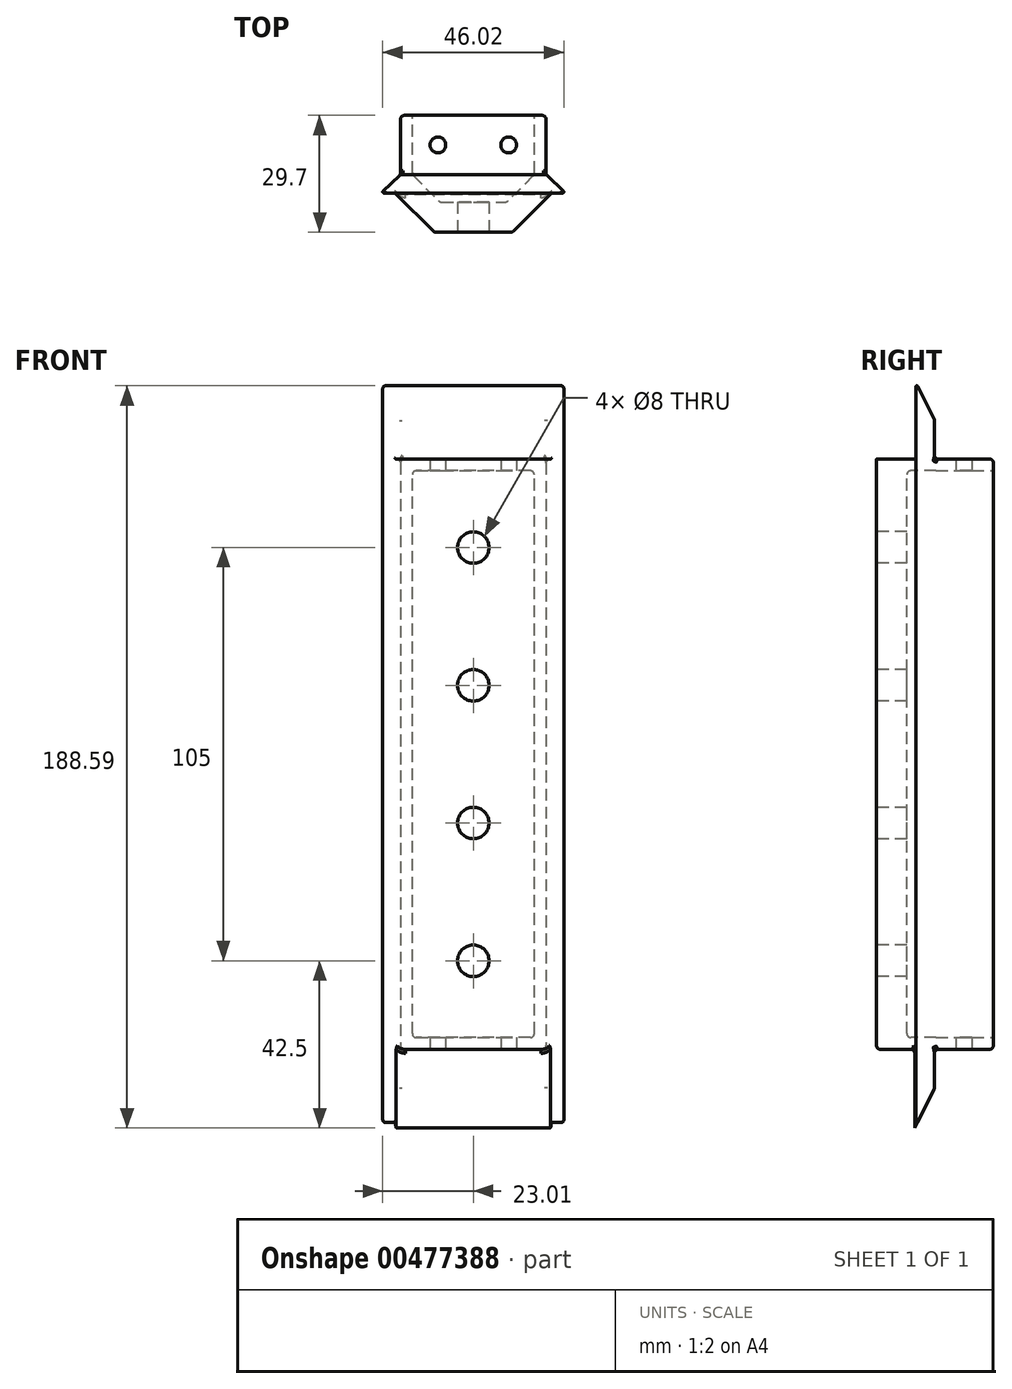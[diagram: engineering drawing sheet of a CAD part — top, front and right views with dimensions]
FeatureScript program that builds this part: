
annotation { "Feature Type Name" : "Feature", "Feature Type Description" : "" }
export const myFeature = defineFeature(function(context is Context, id is Id, definition is map)
    precondition{}
    {
        {
            var Q0;
            Q0=qCreatedBy(makeId("Top.planeOp"),FACE);
            var sketch = newSketch(context, id + "F0", { "sketchPlane" : qUnion([Q0])});
            skLineSegment(sketch, "E0", {"start": v(0, 37.2) * mm, "end": v(0, -38.8) * mm, "construction": true});
            skLineSegment(sketch, "E1", {"start": v(-30.9, 0) * mm, "end": v(40.1, 0) * mm, "construction": true});
            skLineSegment(sketch, "E2.bottom", {"start": v(-18.5, 2.5) * mm, "end": v(18.5, 2.5) * mm});
            skLineSegment(sketch, "E2.top", {"start": v(-23.69, -2.5) * mm, "end": v(23.69, -2.5) * mm});
            skLineSegment(sketch, "E3", {"start": v(-23.69, -2.5) * mm, "end": v(-18.5, 2.5) * mm});
            skLineSegment(sketch, "E4.MirrorCS", {"start": v(23.69, -2.5) * mm, "end": v(18.5, 2.5) * mm});
            skSolve(sketch);
        }
        {
            var Q0;
            Q0 = qSketchRegion(id + "F0", true);
            extrude(context, id + "F1", {"entities" : qUnion([Q0]), "depth" : 170 * mm, "symmetric" : true});
        }
        {
            var Q0;
            Q0=makeQuery(id+"F1.opExtrude","CAP_FACE",FACE,{"disambiguationData":[OSD([sQuery(id+"F0.wireOp",EDGE,"E2.bottom"),sQuery(id+"F0.wireOp",EDGE,"E2.top"),sQuery(id+"F0.wireOp",EDGE,"E3"),sQuery(id+"F0.wireOp",EDGE,"E4.MirrorCS")])],"isStart":false});
            var sketch = newSketch(context, id + "F2", { "sketchPlane" : qUnion([Q0])});
            skLineSegment(sketch, "E5", {"start": v(0, 54.86) * mm, "end": v(0, -60.8) * mm, "construction": true});
            skPoint(sketch, "E5.endSnap0", {"position": v(0, -2.5) * mm});
            skLineSegment(sketch, "E6", {"start": v(20, 2.5) * mm, "end": v(10, 12.5) * mm, "construction": true});
            skLineSegment(sketch, "E7", {"start": v(10, 12.5) * mm, "end": v(0, 12.5) * mm, "construction": true});
            skLineSegment(sketch, "E8.0", {"start": v(-20, 2.5) * mm, "end": v(20, 2.5) * mm, "construction": true});
            skLineSegment(sketch, "E9.MirrorCS", {"start": v(-20, 2.5) * mm, "end": v(-10, 12.5) * mm, "construction": true});
            skLineSegment(sketch, "E10.MirrorCS", {"start": v(-10, 12.5) * mm, "end": v(0, 12.5) * mm, "construction": true});
            skPoint(sketch, "E11.orphan", {"position": v(18.5, 2.5) * mm});
            skPoint(sketch, "E12.orphan", {"position": v(-18.5, 2.5) * mm});
            skLineSegment(sketch, "E13", {"start": v(0, 0) * mm, "end": v(27.86, 0) * mm, "construction": true});
            skPoint(sketch, "E13.endSnap0", {"position": v(21.1, 0) * mm});
            skLineSegment(sketch, "E14.MirrorCS", {"start": v(-20, -2.5) * mm, "end": v(-10, -12.5) * mm});
            skLineSegment(sketch, "E15.MirrorCS", {"start": v(-20, -2.5) * mm, "end": v(20, -2.5) * mm});
            skLineSegment(sketch, "E16.MirrorCS", {"start": v(10, -12.5) * mm, "end": v(0, -12.5) * mm});
            skLineSegment(sketch, "E17.MirrorCS", {"start": v(-10, -12.5) * mm, "end": v(0, -12.5) * mm});
            skLineSegment(sketch, "E18.MirrorCS", {"start": v(20, -2.5) * mm, "end": v(10, -12.5) * mm});
            skPoint(sketch, "E19.MirrorP", {"position": v(18.5, -2.5) * mm});
            skSolve(sketch);
        }
        {
            var Q0;
            Q0 = qSketchRegion(id + "F2", true);
            extrude(context, id + "F3", {"entities" : qUnion([Q0]), "operationType" : NewBodyOperationType.ADD, "oppositeDirection" : true, "depth" : 170 * mm});
        }
        {
            var Q0;
            Q0=qCreatedBy(makeId("Right.planeOp"),FACE);
            var sketch = newSketch(context, id + "F4", { "sketchPlane" : qUnion([Q0])});
            skLineSegment(sketch, "E20", {"start": v(0, 0) * mm, "end": v(-132.45, 0) * mm, "construction": true});
            skLineSegment(sketch, "E21.0", {"start": v(2.5, 75) * mm, "end": v(2.5, -75) * mm});
            skLineSegment(sketch, "E22", {"start": v(2.5, 75) * mm, "end": v(17.5, 75) * mm});
            skLineSegment(sketch, "E23", {"start": v(17.5, 75) * mm, "end": v(17.5, 0) * mm});
            skPoint(sketch, "E24.orphan", {"position": v(2.5, 85) * mm});
            skLineSegment(sketch, "E25.MirrorCS", {"start": v(2.5, -75) * mm, "end": v(17.5, -75) * mm});
            skLineSegment(sketch, "E26.MirrorCS", {"start": v(17.5, -75) * mm, "end": v(17.5, 0) * mm});
            skPoint(sketch, "E27.orphan", {"position": v(2.5, -85) * mm});
            skSolve(sketch);
        }
        {
            var Q0;
            Q0 = qSketchRegion(id + "F4", true);
            extrude(context, id + "F5", {"entities" : qUnion([Q0]), "operationType" : NewBodyOperationType.ADD, "depth" : 37 * mm, "symmetric" : true});
        }
        {
            var Q0;
            Q0=makeQuery(id+"F3.opExtrude","SWEPT_FACE",FACE,{"disambiguationData":[OSD([sQuery(id+"F2.wireOp",EDGE,"E16.MirrorCS"),sQuery(id+"F2.wireOp",EDGE,"E17.MirrorCS")])]});
            var sketch = newSketch(context, id + "F6", { "sketchPlane" : qUnion([Q0])});
            skLineSegment(sketch, "E28", {"start": v(0, 85) * mm, "end": v(0, -85) * mm, "construction": true});
            skCircle(sketch, "E29", {"center": v(0, 52.5) * mm, "radius": 4 * mm});
            skCircle(sketch, "E30", {"center": v(0, 17.5) * mm, "radius": 4 * mm});
            skLineSegment(sketch, "E31", {"start": v(-48.17, 0) * mm, "end": v(56.97, 0) * mm, "construction": true});
            skCircle(sketch, "E32.MirrorC", {"center": v(0, -52.5) * mm, "radius": 4 * mm});
            skCircle(sketch, "E33.MirrorC", {"center": v(0, -17.5) * mm, "radius": 4 * mm});
            skSolve(sketch);
        }
        {
            var Q0;
            Q0 = qSketchRegion(id + "F6", true);
            extrude(context, id + "F7", {"entities" : qUnion([Q0]), "operationType" : NewBodyOperationType.REMOVE, "endBound" : BoundingType.THROUGH_ALL, "oppositeDirection" : true, "depth" : 25 * mm});
        }
        {
            var Q0;
            Q0=makeQuery(id+"F5.opExtrude","SWEPT_FACE",FACE,{"disambiguationData":[OSD([sQuery(id+"F4.wireOp",EDGE,"E23"),sQuery(id+"F4.wireOp",EDGE,"E26.MirrorCS")])]});
            var sketch = newSketch(context, id + "F8", { "sketchPlane" : qUnion([Q0])});
            skLineSegment(sketch, "E34.0", {"start": v(-15.5, -72) * mm, "end": v(-15.5, 72) * mm});
            skLineSegment(sketch, "E34.1", {"start": v(-15.5, -72) * mm, "end": v(15.5, -72) * mm});
            skLineSegment(sketch, "E34.2", {"start": v(15.5, -72) * mm, "end": v(15.5, 72) * mm});
            skLineSegment(sketch, "E34.3", {"start": v(-15.5, 72) * mm, "end": v(15.5, 72) * mm});
            skSolve(sketch);
        }
        {
            var Q0;
            Q0 = qSketchRegion(id + "F8", true);
            var Q1;
            {var subQ2=sQuery(id+"F0.wireOp",EDGE,"E2.bottom");var subQ6=sQuery(id+"F4.wireOp",EDGE,"E22");Q1=makeQuery(id+"F5.boolean.opBoolean","SPLIT",FACE,{"disambiguationData":[TD([makeQuery(id+"F5.opExtrude","SWEPT_FACE",FACE,{"disambiguationData":[OSD([subQ6])]})])],"derivedFrom":makeQuery(id+"F1.opExtrude","SWEPT_FACE",FACE,{"disambiguationData":[OSD([subQ2])]})});}
            extrude(context, id + "F9", {"entities" : qUnion([Q0]), "operationType" : NewBodyOperationType.REMOVE, "endBound" : BoundingType.UP_TO_SURFACE, "oppositeDirection" : true, "endBoundEntityFace" : qUnion([Q1]), "depth" : 25 * mm});
        }
        {
            var Q0;
            Q0=makeQuery(id+"F9.boolean.opBoolean","COPY",FACE,{"derivedFrom":makeQuery(id+"F9.opExtrude","SWEPT_FACE",FACE,{"disambiguationData":[OSD([sQuery(id+"F8.wireOp",EDGE,"E34.3")])]})});
            var sketch = newSketch(context, id + "F10", { "sketchPlane" : qUnion([Q0])});
            skLineSegment(sketch, "E35.0", {"start": v(-15.5, -2.5) * mm, "end": v(-8.5, 4.5) * mm});
            skLineSegment(sketch, "E35.2", {"start": v(15.5, -2.5) * mm, "end": v(8.5, 4.5) * mm});
            skLineSegment(sketch, "E36.0", {"start": v(-15.5, -2.5) * mm, "end": v(15.5, -2.5) * mm});
            skPoint(sketch, "E37.orphan", {"position": v(15.5, -2.5) * mm});
            skPoint(sketch, "E38.orphan", {"position": v(-15.5, -2.5) * mm});
            skLineSegment(sketch, "E39.0", {"start": v(-8.5, 4.5) * mm, "end": v(8.5, 4.5) * mm});
            skSolve(sketch);
        }
        {
            var Q0;
            Q0 = qSketchRegion(id + "F10", true);
            var Q1;
            Q1=makeQuery(id+"F9.boolean.opBoolean","COPY",FACE,{"derivedFrom":makeQuery(id+"F9.opExtrude","SWEPT_FACE",FACE,{"disambiguationData":[OSD([sQuery(id+"F8.wireOp",EDGE,"E34.1")])]})});
            extrude(context, id + "F11", {"entities" : qUnion([Q0]), "operationType" : NewBodyOperationType.REMOVE, "endBound" : BoundingType.UP_TO_SURFACE, "endBoundEntityFace" : qUnion([Q1]), "depth" : 25 * mm});
        }
        {
            var Q0;
            Q0=makeQuery(id+"F5.opExtrude","SWEPT_FACE",FACE,{"disambiguationData":[OSD([sQuery(id+"F4.wireOp",EDGE,"E25.MirrorCS")])]});
            var sketch = newSketch(context, id + "F12", { "sketchPlane" : qUnion([Q0])});
            skLineSegment(sketch, "E40.0", {"start": v(-15.5, -2.5) * mm, "end": v(-15.5, -17.5) * mm, "construction": true});
            skLineSegment(sketch, "E40.1", {"start": v(15.5, -2.5) * mm, "end": v(15.5, -17.5) * mm, "construction": true});
            skLineSegment(sketch, "E41", {"start": v(-15.5, -10) * mm, "end": v(15.5, -10) * mm, "construction": true});
            skCircle(sketch, "E42", {"center": v(-9, -10) * mm, "radius": 2 * mm});
            skLineSegment(sketch, "E43", {"start": v(0, -2.5) * mm, "end": v(0, -17.5) * mm, "construction": true});
            skCircle(sketch, "E44.MirrorC", {"center": v(9, -10) * mm, "radius": 2 * mm});
            skCircle(sketch, "E45", {"center": v(9, -10) * mm, "radius": 3.5 * mm, "construction": true});
            skSolve(sketch);
        }
        {
            var Q0;
            Q0=makeQuery(id+"F3.boolean.opBoolean","MERGE",FACE,{"derivedFrom":[makeQuery(id+"F1.opExtrude","CAP_FACE",FACE,{"disambiguationData":[OSD([sQuery(id+"F0.wireOp",EDGE,"E2.bottom"),sQuery(id+"F0.wireOp",EDGE,"E2.top"),sQuery(id+"F0.wireOp",EDGE,"E3"),sQuery(id+"F0.wireOp",EDGE,"E4.MirrorCS")])],"isStart":true}),makeQuery(id+"F3.opExtrude","CAP_FACE",FACE,{"disambiguationData":[OSD([sQuery(id+"F2.wireOp",EDGE,"E14.MirrorCS"),sQuery(id+"F2.wireOp",EDGE,"E15.MirrorCS"),sQuery(id+"F2.wireOp",EDGE,"E16.MirrorCS"),sQuery(id+"F2.wireOp",EDGE,"E17.MirrorCS"),sQuery(id+"F2.wireOp",EDGE,"E18.MirrorCS")])],"isStart":false})]});
            var sketch = newSketch(context, id + "F13", { "sketchPlane" : qUnion([Q0])});
            skLineSegment(sketch, "E46.0", {"start": v(20, 2.5) * mm, "end": v(10, 12.5) * mm});
            skLineSegment(sketch, "E46.1", {"start": v(-10, 12.5) * mm, "end": v(10, 12.5) * mm});
            skLineSegment(sketch, "E46.2", {"start": v(-20, 2.5) * mm, "end": v(-10, 12.5) * mm});
            skPoint(sketch, "E46.3", {"position": v(15, 7.5) * mm});
            skLineSegment(sketch, "E47", {"start": v(20, 2.5) * mm, "end": v(-20, 2.5) * mm});
            skSolve(sketch);
        }
        {
            var Q0;
            Q0 = qSketchRegion(id + "F13", true);
            extrude(context, id + "F14", {"entities" : qUnion([Q0]), "operationType" : NewBodyOperationType.REMOVE, "oppositeDirection" : true, "depth" : 10 * mm});
        }
        {
            var Q0;
            Q0=makeQuery(id+"F3.boolean.opBoolean","MERGE",FACE,{"derivedFrom":[makeQuery(id+"F1.opExtrude","CAP_FACE",FACE,{"disambiguationData":[OSD([sQuery(id+"F0.wireOp",EDGE,"E2.bottom"),sQuery(id+"F0.wireOp",EDGE,"E2.top"),sQuery(id+"F0.wireOp",EDGE,"E3"),sQuery(id+"F0.wireOp",EDGE,"E4.MirrorCS")])],"isStart":false}),makeQuery(id+"F3.opExtrude","CAP_FACE",FACE,{"disambiguationData":[OSD([sQuery(id+"F2.wireOp",EDGE,"E14.MirrorCS"),sQuery(id+"F2.wireOp",EDGE,"E15.MirrorCS"),sQuery(id+"F2.wireOp",EDGE,"E16.MirrorCS"),sQuery(id+"F2.wireOp",EDGE,"E17.MirrorCS"),sQuery(id+"F2.wireOp",EDGE,"E18.MirrorCS")])],"isStart":true})]});
            var sketch = newSketch(context, id + "F15", { "sketchPlane" : qUnion([Q0])});
            skLineSegment(sketch, "E48.0", {"start": v(20, -2.5) * mm, "end": v(10, -12.5) * mm});
            skLineSegment(sketch, "E48.1", {"start": v(-10, -12.5) * mm, "end": v(10, -12.5) * mm});
            skLineSegment(sketch, "E48.2", {"start": v(-20, -2.5) * mm, "end": v(-10, -12.5) * mm});
            skLineSegment(sketch, "E49", {"start": v(20, -2.5) * mm, "end": v(-20, -2.5) * mm});
            skSolve(sketch);
        }
        {
            var Q0;
            Q0 = qSketchRegion(id + "F15", true);
            extrude(context, id + "F16", {"entities" : qUnion([Q0]), "operationType" : NewBodyOperationType.REMOVE, "oppositeDirection" : true, "depth" : 10 * mm});
        }
        {
            var Q0;
            Q0 = qSketchRegion(id + "F12", true);
            extrude(context, id + "F17", {"entities" : qUnion([Q0]), "operationType" : NewBodyOperationType.REMOVE, "endBound" : BoundingType.THROUGH_ALL, "oppositeDirection" : true, "depth" : 25 * mm});
        }
        {
            var Q0;
            Q0=makeQuery(id+"F3.boolean.opBoolean","MERGE",FACE,{"derivedFrom":[makeQuery(id+"F1.opExtrude","CAP_FACE",FACE,{"disambiguationData":[OSD([sQuery(id+"F0.wireOp",EDGE,"E2.bottom"),sQuery(id+"F0.wireOp",EDGE,"E2.top"),sQuery(id+"F0.wireOp",EDGE,"E3"),sQuery(id+"F0.wireOp",EDGE,"E4.MirrorCS")])],"isStart":false}),makeQuery(id+"F3.opExtrude","CAP_FACE",FACE,{"disambiguationData":[OSD([sQuery(id+"F2.wireOp",EDGE,"E14.MirrorCS"),sQuery(id+"F2.wireOp",EDGE,"E15.MirrorCS"),sQuery(id+"F2.wireOp",EDGE,"E16.MirrorCS"),sQuery(id+"F2.wireOp",EDGE,"E17.MirrorCS"),sQuery(id+"F2.wireOp",EDGE,"E18.MirrorCS")])],"isStart":true})]});
            extrude(context, id + "F18", {"entities" : qUnion([Q0]), "operationType" : NewBodyOperationType.ADD, "depth" : 10 * mm});
        }
        {
            var Q0;
            Q0=makeQuery(id+"F3.boolean.opBoolean","MERGE",FACE,{"derivedFrom":[makeQuery(id+"F1.opExtrude","CAP_FACE",FACE,{"disambiguationData":[OSD([sQuery(id+"F0.wireOp",EDGE,"E2.bottom"),sQuery(id+"F0.wireOp",EDGE,"E2.top"),sQuery(id+"F0.wireOp",EDGE,"E3"),sQuery(id+"F0.wireOp",EDGE,"E4.MirrorCS")])],"isStart":true}),makeQuery(id+"F3.opExtrude","CAP_FACE",FACE,{"disambiguationData":[OSD([sQuery(id+"F2.wireOp",EDGE,"E14.MirrorCS"),sQuery(id+"F2.wireOp",EDGE,"E15.MirrorCS"),sQuery(id+"F2.wireOp",EDGE,"E16.MirrorCS"),sQuery(id+"F2.wireOp",EDGE,"E17.MirrorCS"),sQuery(id+"F2.wireOp",EDGE,"E18.MirrorCS")])],"isStart":false})]});
            extrude(context, id + "F19", {"entities" : qUnion([Q0]), "operationType" : NewBodyOperationType.ADD, "depth" : 10 * mm});
        }
        {
            var Q0;
            Q0=makeQuery(id+"F18.opExtrude","CAP_EDGE",EDGE,{"disambiguationData":[OSD([sQuery(id+"F0.wireOp",EDGE,"E2.bottom")])],"isStart":false});
            chamfer(context, id + "F20", {"entities" : qUnion([Q0]), "chamferType" : ChamferType.TWO_OFFSETS, "width1" : 5 * mm, "oppositeDirection" : true, "width2" : 10 * mm, "tangentPropagation" : true});
        }
        {
            var Q0;
            Q0=makeQuery(id+"F19.opExtrude","CAP_EDGE",EDGE,{"disambiguationData":[OSD([sQuery(id+"F0.wireOp",EDGE,"E2.bottom")])],"isStart":false});
            chamfer(context, id + "F21", {"entities" : qUnion([Q0]), "chamferType" : ChamferType.TWO_OFFSETS, "width1" : 10 * mm, "oppositeDirection" : true, "width2" : 5 * mm, "tangentPropagation" : true});
        }
        {
            var Q0;
            Q0=makeQuery(id+"F16.boolean.opBoolean","COPY",FACE,{"derivedFrom":makeQuery(id+"F16.opExtrude","CAP_FACE",FACE,{"disambiguationData":[OSD([sQuery(id+"F15.wireOp",EDGE,"E48.0"),sQuery(id+"F15.wireOp",EDGE,"E48.1"),sQuery(id+"F15.wireOp",EDGE,"E48.2"),sQuery(id+"F15.wireOp",EDGE,"E49")])],"isStart":false})});
            var sketch = newSketch(context, id + "F22", { "sketchPlane" : qUnion([Q0])});
            skLineSegment(sketch, "E50.0", {"start": v(-19.58, -2.5) * mm, "end": v(-9.88, -12.2) * mm});
            skLineSegment(sketch, "E50.1", {"start": v(-9.88, -12.2) * mm, "end": v(9.88, -12.2) * mm});
            skLineSegment(sketch, "E50.2", {"start": v(19.58, -2.5) * mm, "end": v(9.88, -12.2) * mm});
            skLineSegment(sketch, "E51.0", {"start": v(-23.69, -2.5) * mm, "end": v(-19.58, -2.5) * mm});
            skLineSegment(sketch, "E52", {"start": v(-23.69, -2.5) * mm, "end": v(-23.69, -16.5) * mm});
            skLineSegment(sketch, "E53", {"start": v(-23.69, -16.5) * mm, "end": v(23.69, -16.5) * mm});
            skLineSegment(sketch, "E54", {"start": v(23.69, -16.5) * mm, "end": v(23.69, -2.5) * mm});
            skLineSegment(sketch, "E55.trimOffspring", {"start": v(19.58, -2.5) * mm, "end": v(23.69, -2.5) * mm});
            skSolve(sketch);
        }
        {
            var Q0;
            Q0 = qSketchRegion(id + "F22", true);
            extrude(context, id + "F23", {"entities" : qUnion([Q0]), "operationType" : NewBodyOperationType.REMOVE, "endBound" : BoundingType.THROUGH_ALL, "oppositeDirection" : true, "depth" : 25 * mm});
        }
        {
            var Q0;
            Q0=qCreatedBy(makeId("Top.planeOp"),FACE);
            var sketch = newSketch(context, id + "F24", { "sketchPlane" : qUnion([Q0])});
            skLineSegment(sketch, "E56.0", {"start": v(-23.38, -2.2) * mm, "end": v(-19.88, -2.2) * mm});
            skLineSegment(sketch, "E57.0", {"start": v(-23.69, -2.5) * mm, "end": v(-19.58, -2.5) * mm});
            skLineSegment(sketch, "E57.1", {"start": v(-23.69, -2.5) * mm, "end": v(-23.38, -2.2) * mm});
            skLineSegment(sketch, "E58.trimOffspring", {"start": v(-19.88, -2.2) * mm, "end": v(-19.58, -2.5) * mm});
            skPoint(sketch, "E59.orphan", {"position": v(-18.5, 2.5) * mm});
            skPoint(sketch, "E60.orphan", {"position": v(-9.88, -12.2) * mm});
            skLineSegment(sketch, "E61", {"start": v(-9.88, -12.2) * mm, "end": v(9.88, -12.2) * mm, "construction": true});
            skLineSegment(sketch, "E62", {"start": v(0, -12.2) * mm, "end": v(0, 15.52) * mm, "construction": true});
            skLineSegment(sketch, "E63.MirrorCS", {"start": v(19.88, -2.2) * mm, "end": v(19.58, -2.5) * mm});
            skLineSegment(sketch, "E64.MirrorCS", {"start": v(23.69, -2.5) * mm, "end": v(23.38, -2.2) * mm});
            skLineSegment(sketch, "E65.MirrorCS", {"start": v(23.69, -2.5) * mm, "end": v(19.58, -2.5) * mm});
            skLineSegment(sketch, "E66.MirrorCS", {"start": v(23.38, -2.2) * mm, "end": v(19.88, -2.2) * mm});
            skSolve(sketch);
        }
        {
            var Q0;
            Q0 = qSketchRegion(id + "F24", true);
            extrude(context, id + "F25", {"entities" : qUnion([Q0]), "operationType" : NewBodyOperationType.REMOVE, "oppositeDirection" : true, "depth" : 200 * mm, "symmetric" : true});
        }
        {
            var Q0;
            Q0=makeQuery(id+"F16.boolean.opBoolean","COPY",FACE,{"derivedFrom":makeQuery(id+"F16.opExtrude","CAP_FACE",FACE,{"disambiguationData":[OSD([sQuery(id+"F15.wireOp",EDGE,"E48.0"),sQuery(id+"F15.wireOp",EDGE,"E48.1"),sQuery(id+"F15.wireOp",EDGE,"E48.2"),sQuery(id+"F15.wireOp",EDGE,"E49")])],"isStart":false})});
            var sketch = newSketch(context, id + "F26", { "sketchPlane" : qUnion([Q0])});
            skLineSegment(sketch, "E67.0", {"start": v(-19.88, -2.2) * mm, "end": v(-19.58, -2.5) * mm});
            skLineSegment(sketch, "E67.1", {"start": v(-19.58, -2.5) * mm, "end": v(19.58, -2.5) * mm});
            skLineSegment(sketch, "E67.2", {"start": v(19.88, -2.2) * mm, "end": v(19.58, -2.5) * mm});
            skLineSegment(sketch, "E68", {"start": v(19.88, -2.2) * mm, "end": v(-19.88, -2.2) * mm});
            skSolve(sketch);
        }
        {
            var Q0;
            Q0 = qSketchRegion(id + "F26", true);
            extrude(context, id + "F27", {"entities" : qUnion([Q0]), "operationType" : NewBodyOperationType.REMOVE, "depth" : 25 * mm});
        }
        {
            var Q0;
            {var subQ0=sQuery(id+"F8.wireOp",EDGE,"E34.2");Q0=makeQuery(id+"F11.boolean.opBoolean","MERGE",EDGE,{"derivedFrom":[makeQuery(id+"F9.boolean.opBoolean","COPY",EDGE,{"derivedFrom":makeQuery(id+"F9.opExtrude","CAP_EDGE",EDGE,{"disambiguationData":[OSD([subQ0])],"isStart":false})}),makeQuery(id+"F11.opExtrude","SWEPT_EDGE",EDGE,{"disambiguationData":[OSD([subQ0,sQuery(id+"F8.wireOp",EDGE,"E34.3"),sQuery(id+"F10.wireOp",EDGE,"E35.0"),sQuery(id+"F10.wireOp",EDGE,"E36.0")])]})]});}
            var Q1;
            Q1=makeQuery(id+"F11.boolean.opBoolean","COPY",EDGE,{"derivedFrom":makeQuery(id+"F11.opExtrude","SWEPT_EDGE",EDGE,{"disambiguationData":[OSD([sQuery(id+"F10.wireOp",EDGE,"E35.0"),sQuery(id+"F10.wireOp",EDGE,"E39.0")])]})});
            var Q2;
            Q2=makeQuery(id+"F11.boolean.opBoolean","COPY",EDGE,{"derivedFrom":makeQuery(id+"F11.opExtrude","SWEPT_EDGE",EDGE,{"disambiguationData":[OSD([sQuery(id+"F10.wireOp",EDGE,"E35.2"),sQuery(id+"F10.wireOp",EDGE,"E39.0")])]})});
            var Q3;
            {var subQ0=sQuery(id+"F8.wireOp",EDGE,"E34.0");Q3=makeQuery(id+"F11.boolean.opBoolean","MERGE",EDGE,{"derivedFrom":[makeQuery(id+"F9.boolean.opBoolean","COPY",EDGE,{"derivedFrom":makeQuery(id+"F9.opExtrude","CAP_EDGE",EDGE,{"disambiguationData":[OSD([subQ0])],"isStart":false})}),makeQuery(id+"F11.opExtrude","SWEPT_EDGE",EDGE,{"disambiguationData":[OSD([subQ0,sQuery(id+"F8.wireOp",EDGE,"E34.3"),sQuery(id+"F10.wireOp",EDGE,"E35.2"),sQuery(id+"F10.wireOp",EDGE,"E36.0")])]})]});}
            var Q4;
            Q4=makeQuery(id+"F23.boolean.opBoolean","COPY",EDGE,{"derivedFrom":makeQuery(id+"F23.opExtrude","SWEPT_EDGE",EDGE,{"disambiguationData":[OSD([sQuery(id+"F22.wireOp",EDGE,"E50.0"),sQuery(id+"F22.wireOp",EDGE,"E50.1")])]})});
            var Q5;
            Q5=makeQuery(id+"F23.boolean.opBoolean","COPY",EDGE,{"derivedFrom":makeQuery(id+"F23.opExtrude","SWEPT_EDGE",EDGE,{"disambiguationData":[OSD([sQuery(id+"F22.wireOp",EDGE,"E50.1"),sQuery(id+"F22.wireOp",EDGE,"E50.2")])]})});
            fillet(context, id + "F28", {"entities" : qUnion([Q0, Q1, Q2, Q3, Q4, Q5]), "radius" : 1 * mm, "tangentPropagation" : true, "allowEdgeOverflow" : false});
        }
        {
            var Q0;
            Q0=makeQuery(id+"F16.boolean.opBoolean","COPY",EDGE,{"derivedFrom":makeQuery(id+"F16.opExtrude","CAP_EDGE",EDGE,{"disambiguationData":[OSD([sQuery(id+"F15.wireOp",EDGE,"E48.2")])],"isStart":false})});
            var Q1;
            Q1=makeQuery(id+"F14.boolean.opBoolean","COPY",EDGE,{"derivedFrom":makeQuery(id+"F14.opExtrude","CAP_EDGE",EDGE,{"disambiguationData":[OSD([sQuery(id+"F13.wireOp",EDGE,"E46.2")])],"isStart":false})});
            var Q2;
            Q2=makeQuery(id+"F9.boolean.opBoolean","COPY",EDGE,{"derivedFrom":makeQuery(id+"F9.opExtrude","SWEPT_EDGE",EDGE,{"disambiguationData":[OSD([sQuery(id+"F8.wireOp",EDGE,"E34.0"),sQuery(id+"F8.wireOp",EDGE,"E34.1")])]})});
            var Q3;
            Q3=makeQuery(id+"F9.boolean.opBoolean","COPY",EDGE,{"derivedFrom":makeQuery(id+"F9.opExtrude","SWEPT_EDGE",EDGE,{"disambiguationData":[OSD([sQuery(id+"F8.wireOp",EDGE,"E34.0"),sQuery(id+"F8.wireOp",EDGE,"E34.3")])]})});
            var Q4;
            Q4=makeQuery(id+"F23.boolean.opBoolean","COPY",EDGE,{"derivedFrom":makeQuery(id+"F23.opExtrude","SWEPT_EDGE",EDGE,{"disambiguationData":[OSD([sQuery(id+"F22.wireOp",EDGE,"E50.0"),sQuery(id+"F22.wireOp",EDGE,"E50.1")])]})});
            var Q5;
            Q5=makeQuery(id+"F23.boolean.opBoolean","COPY",EDGE,{"derivedFrom":makeQuery(id+"F23.opExtrude","SWEPT_EDGE",EDGE,{"disambiguationData":[OSD([sQuery(id+"F22.wireOp",EDGE,"E50.1"),sQuery(id+"F22.wireOp",EDGE,"E50.2")])]})});
            fillet(context, id + "F29", {"entities" : qUnion([Q0, Q1, Q2, Q3, Q4, Q5]), "radius" : 1 * mm, "tangentPropagation" : true, "allowEdgeOverflow" : false});
        }
        {
            var Q0;
            Q0=makeQuery(id+"F23.boolean.opBoolean","COPY",EDGE,{"derivedFrom":makeQuery(id+"F23.opExtrude","CAP_EDGE",EDGE,{"disambiguationData":[OSD([sQuery(id+"F22.wireOp",EDGE,"E50.0")])],"isStart":true})});
            var Q1;
            Q1=makeQuery(id+"F23.boolean.opBoolean","INTERSECT",EDGE,{"derivedFrom":[makeQuery(id+"F14.boolean.opBoolean","COPY",FACE,{"derivedFrom":makeQuery(id+"F14.opExtrude","CAP_FACE",FACE,{"disambiguationData":[OSD([sQuery(id+"F13.wireOp",EDGE,"E46.0"),sQuery(id+"F13.wireOp",EDGE,"E46.1"),sQuery(id+"F13.wireOp",EDGE,"E46.2"),sQuery(id+"F13.wireOp",EDGE,"E47")])],"isStart":false})}),makeQuery(id+"F23.opExtrude","SWEPT_FACE",FACE,{"disambiguationData":[OSD([sQuery(id+"F22.wireOp",EDGE,"E50.0")])]})]});
            fillet(context, id + "F30", {"entities" : qUnion([Q0, Q1]), "radius" : 1 * mm, "tangentPropagation" : true, "allowEdgeOverflow" : false});
        }
        {
            var Q0;
            Q0=makeQuery(id+"F14.boolean.opBoolean","COPY",EDGE,{"derivedFrom":makeQuery(id+"F14.opExtrude","CAP_EDGE",EDGE,{"disambiguationData":[OSD([sQuery(id+"F13.wireOp",EDGE,"E47")])],"isStart":false})});
            var Q1;
            Q1=makeQuery(id+"FHIxGTzLpelhpMh_1.1.F27.boolean.opBoolean","COPY",EDGE,{"derivedFrom":makeQuery(id+"FHIxGTzLpelhpMh_1.1.F27.opExtrude","CAP_EDGE",EDGE,{"disambiguationData":[OSD([sQuery(id+"F26.wireOp",EDGE,"E68")])],"isStart":true})});
            fillet(context, id + "F31", {"entities" : qUnion([Q0, Q1]), "radius" : 1 * mm, "tangentPropagation" : true, "allowEdgeOverflow" : false});
        }
        {
            var Q0;
            Q0=makeQuery(id+"F5.opExtrude","CAP_EDGE",EDGE,{"disambiguationData":[OSD([sQuery(id+"F4.wireOp",EDGE,"E22")])],"isStart":false});
            var Q1;
            Q1=makeQuery(id+"F5.opExtrude","CAP_EDGE",EDGE,{"disambiguationData":[OSD([sQuery(id+"F4.wireOp",EDGE,"E22")])],"isStart":true});
            var Q2;
            Q2=makeQuery(id+"F5.opExtrude","CAP_EDGE",EDGE,{"disambiguationData":[OSD([sQuery(id+"F4.wireOp",EDGE,"E25.MirrorCS")])],"isStart":true});
            var Q3;
            Q3=makeQuery(id+"F5.opExtrude","CAP_EDGE",EDGE,{"disambiguationData":[OSD([sQuery(id+"F4.wireOp",EDGE,"E25.MirrorCS")])],"isStart":false});
            fillet(context, id + "F32", {"entities" : qUnion([Q0, Q1, Q2, Q3]), "radius" : 1 * mm, "tangentPropagation" : true, "allowEdgeOverflow" : false});
        }
        {
            var Q0;
            {var subQ0=sQuery(id+"F0.wireOp",EDGE,"E4.MirrorCS");var subQ1=sQuery(id+"F0.wireOp",EDGE,"E2.bottom");var subQ2=sQuery(id+"F4.wireOp",EDGE,"E22");Q0=makeQuery(id+"F5.boolean.opBoolean","SPLIT",EDGE,{"disambiguationData":[TD([makeQuery(id+"F5.opExtrude","SWEPT_FACE",FACE,{"disambiguationData":[OSD([subQ2])]})])],"derivedFrom":makeQuery(id+"F1.opExtrude","SWEPT_EDGE",EDGE,{"disambiguationData":[OSD([subQ1,subQ0])]})});}
            var Q1;
            {var subQ0=sQuery(id+"F0.wireOp",EDGE,"E4.MirrorCS");var subQ1=sQuery(id+"F0.wireOp",EDGE,"E2.bottom");var subQ2=sQuery(id+"F4.wireOp",EDGE,"E25.MirrorCS");Q1=makeQuery(id+"F5.boolean.opBoolean","SPLIT",EDGE,{"disambiguationData":[TD([makeQuery(id+"F5.opExtrude","SWEPT_FACE",FACE,{"disambiguationData":[OSD([subQ2])]})])],"derivedFrom":makeQuery(id+"F1.opExtrude","SWEPT_EDGE",EDGE,{"disambiguationData":[OSD([subQ1,subQ0])]})});}
            var Q2;
            {var subQ0=sQuery(id+"F0.wireOp",EDGE,"E3");var subQ1=sQuery(id+"F0.wireOp",EDGE,"E2.bottom");var subQ2=sQuery(id+"F4.wireOp",EDGE,"E25.MirrorCS");Q2=makeQuery(id+"F5.boolean.opBoolean","SPLIT",EDGE,{"disambiguationData":[TD([makeQuery(id+"F5.opExtrude","SWEPT_FACE",FACE,{"disambiguationData":[OSD([subQ2])]})])],"derivedFrom":makeQuery(id+"F1.opExtrude","SWEPT_EDGE",EDGE,{"disambiguationData":[OSD([subQ1,subQ0])]})});}
            var Q3;
            {var subQ0=sQuery(id+"F0.wireOp",EDGE,"E3");var subQ1=sQuery(id+"F0.wireOp",EDGE,"E2.bottom");var subQ2=sQuery(id+"F4.wireOp",EDGE,"E22");Q3=makeQuery(id+"F5.boolean.opBoolean","SPLIT",EDGE,{"disambiguationData":[TD([makeQuery(id+"F5.opExtrude","SWEPT_FACE",FACE,{"disambiguationData":[OSD([subQ2])]})])],"derivedFrom":makeQuery(id+"F1.opExtrude","SWEPT_EDGE",EDGE,{"disambiguationData":[OSD([subQ1,subQ0])]})});}
            fillet(context, id + "F33", {"entities" : qUnion([Q0, Q1, Q2, Q3]), "radius" : 1 * mm, "tangentPropagation" : true, "allowEdgeOverflow" : false});
        }
        {
            var Q0;
            {var subQ0=sQuery(id+"F0.wireOp",EDGE,"E4.MirrorCS");Q0=makeQuery(id+"F20.opChamfer","BLEND_EDGE",EDGE,{"blendedFrom":[makeQuery(id+"F18.opExtrude","CAP_EDGE",EDGE,{"disambiguationData":[OSD([sQuery(id+"F0.wireOp",EDGE,"E2.bottom")])],"isStart":false}),makeQuery(id+"F19.boolean.opBoolean","MERGE",FACE,{"derivedFrom":[makeQuery(id+"F18.boolean.opBoolean","MERGE",FACE,{"derivedFrom":[makeQuery(id+"F1.opExtrude","SWEPT_FACE",FACE,{"disambiguationData":[OSD([subQ0])]}),makeQuery(id+"F18.opExtrude","SWEPT_FACE",FACE,{"disambiguationData":[OSD([subQ0])]})]}),makeQuery(id+"F19.opExtrude","SWEPT_FACE",FACE,{"disambiguationData":[OSD([subQ0])]})]})],"blendedInto":[makeQuery(id+"F19.boolean.opBoolean","MERGE",FACE,{"derivedFrom":[makeQuery(id+"F18.boolean.opBoolean","MERGE",FACE,{"derivedFrom":[makeQuery(id+"F1.opExtrude","SWEPT_FACE",FACE,{"disambiguationData":[OSD([subQ0])]}),makeQuery(id+"F18.opExtrude","SWEPT_FACE",FACE,{"disambiguationData":[OSD([subQ0])]})]}),makeQuery(id+"F19.opExtrude","SWEPT_FACE",FACE,{"disambiguationData":[OSD([subQ0])]})]})]});}
            var Q1;
            {var subQ0=sQuery(id+"F0.wireOp",EDGE,"E4.MirrorCS");Q1=makeQuery(id+"F21.opChamfer","BLEND_EDGE",EDGE,{"blendedFrom":[makeQuery(id+"F19.opExtrude","CAP_EDGE",EDGE,{"disambiguationData":[OSD([sQuery(id+"F0.wireOp",EDGE,"E2.bottom")])],"isStart":false}),makeQuery(id+"F19.boolean.opBoolean","MERGE",FACE,{"derivedFrom":[makeQuery(id+"F18.boolean.opBoolean","MERGE",FACE,{"derivedFrom":[makeQuery(id+"F1.opExtrude","SWEPT_FACE",FACE,{"disambiguationData":[OSD([subQ0])]}),makeQuery(id+"F18.opExtrude","SWEPT_FACE",FACE,{"disambiguationData":[OSD([subQ0])]})]}),makeQuery(id+"F19.opExtrude","SWEPT_FACE",FACE,{"disambiguationData":[OSD([subQ0])]})]})],"blendedInto":[makeQuery(id+"F19.boolean.opBoolean","MERGE",FACE,{"derivedFrom":[makeQuery(id+"F18.boolean.opBoolean","MERGE",FACE,{"derivedFrom":[makeQuery(id+"F1.opExtrude","SWEPT_FACE",FACE,{"disambiguationData":[OSD([subQ0])]}),makeQuery(id+"F18.opExtrude","SWEPT_FACE",FACE,{"disambiguationData":[OSD([subQ0])]})]}),makeQuery(id+"F19.opExtrude","SWEPT_FACE",FACE,{"disambiguationData":[OSD([subQ0])]})]})]});}
            fillet(context, id + "F34", {"entities" : qUnion([Q0, Q1]), "radius" : 1 * mm, "tangentPropagation" : true, "allowEdgeOverflow" : false});
        }
        {
            var Q0;
            Q0=makeQuery(id+"F5.opExtrude","SWEPT_EDGE",EDGE,{"disambiguationData":[OSD([sQuery(id+"F4.wireOp",EDGE,"E21.0"),sQuery(id+"F4.wireOp",EDGE,"E25.MirrorCS")])]});
            var Q1;
            Q1=makeQuery(id+"F5.opExtrude","SWEPT_EDGE",EDGE,{"disambiguationData":[OSD([sQuery(id+"F4.wireOp",EDGE,"E21.0"),sQuery(id+"F4.wireOp",EDGE,"E22")])]});
            var Q2;
            Q2=makeQuery(id+"F5.opExtrude","SWEPT_EDGE",EDGE,{"disambiguationData":[OSD([sQuery(id+"F4.wireOp",EDGE,"E22"),sQuery(id+"F4.wireOp",EDGE,"E23")])]});
            var Q3;
            Q3=makeQuery(id+"F9.boolean.opBoolean","COPY",EDGE,{"derivedFrom":makeQuery(id+"F9.opExtrude","CAP_EDGE",EDGE,{"disambiguationData":[OSD([sQuery(id+"F8.wireOp",EDGE,"E34.3")])],"isStart":true})});
            var Q4;
            Q4=makeQuery(id+"F5.boolean.opBoolean","MERGE",EDGE,{"derivedFrom":[makeQuery(id+"F1.opExtrude","SWEPT_EDGE",EDGE,{"disambiguationData":[OSD([sQuery(id+"F0.wireOp",EDGE,"E2.bottom"),sQuery(id+"F0.wireOp",EDGE,"E3")])]}),makeQuery(id+"F5.opExtrude","CAP_EDGE",EDGE,{"disambiguationData":[OSD([sQuery(id+"F4.wireOp",EDGE,"E21.0")])],"isStart":true})]});
            var Q5;
            Q5=makeQuery(id+"F5.boolean.opBoolean","MERGE",EDGE,{"derivedFrom":[makeQuery(id+"F1.opExtrude","SWEPT_EDGE",EDGE,{"disambiguationData":[OSD([sQuery(id+"F0.wireOp",EDGE,"E2.bottom"),sQuery(id+"F0.wireOp",EDGE,"E4.MirrorCS")])]}),makeQuery(id+"F5.opExtrude","CAP_EDGE",EDGE,{"disambiguationData":[OSD([sQuery(id+"F4.wireOp",EDGE,"E21.0")])],"isStart":false})]});
            fillet(context, id + "F35", {"entities" : qUnion([Q0, Q1, Q2, Q3, Q4, Q5]), "radius" : 1 * mm, "tangentPropagation" : true, "allowEdgeOverflow" : false});
        }
        {
            var Q0;
            Q0=makeQuery(id+"F1.opExtrude","SWEPT_EDGE",EDGE,{"disambiguationData":[OSD([sQuery(id+"F0.wireOp",EDGE,"E2.top"),sQuery(id+"F0.wireOp",EDGE,"E4.MirrorCS")])]});
            var Q1;
            Q1=makeQuery(id+"F1.opExtrude","SWEPT_EDGE",EDGE,{"disambiguationData":[OSD([sQuery(id+"F0.wireOp",EDGE,"E2.top"),sQuery(id+"F0.wireOp",EDGE,"E3")])]});
            var Q2;
            {var subQ0=sQuery(id+"F26.wireOp",EDGE,"E68");Q2=makeQuery(id+"FHIxGTzLpelhpMh_1.1.F27.boolean.opBoolean","MERGE",FACE,{"derivedFrom":[makeQuery(id+"F27.boolean.opBoolean","MERGE",FACE,{"derivedFrom":[makeQuery(id+"F25.boolean.opBoolean","COPY",FACE,{"derivedFrom":makeQuery(id+"F25.opExtrude","SWEPT_FACE",FACE,{"disambiguationData":[OSD([sQuery(id+"F24.wireOp",EDGE,"E56.0")])]})}),makeQuery(id+"F25.boolean.opBoolean","COPY",FACE,{"derivedFrom":makeQuery(id+"F25.opExtrude","SWEPT_FACE",FACE,{"disambiguationData":[OSD([sQuery(id+"F24.wireOp",EDGE,"E66.MirrorCS")])]})}),makeQuery(id+"F27.opExtrude","SWEPT_FACE",FACE,{"disambiguationData":[OSD([subQ0])]})]}),makeQuery(id+"FHIxGTzLpelhpMh_1.1.F27.opExtrude","SWEPT_FACE",FACE,{"disambiguationData":[OSD([subQ0])]})]});}
            fillet(context, id + "F36", {"entities" : qUnion([Q0, Q1, Q2]), "radius" : 0.25 * mm, "tangentPropagation" : true, "allowEdgeOverflow" : false});
        }
    });
